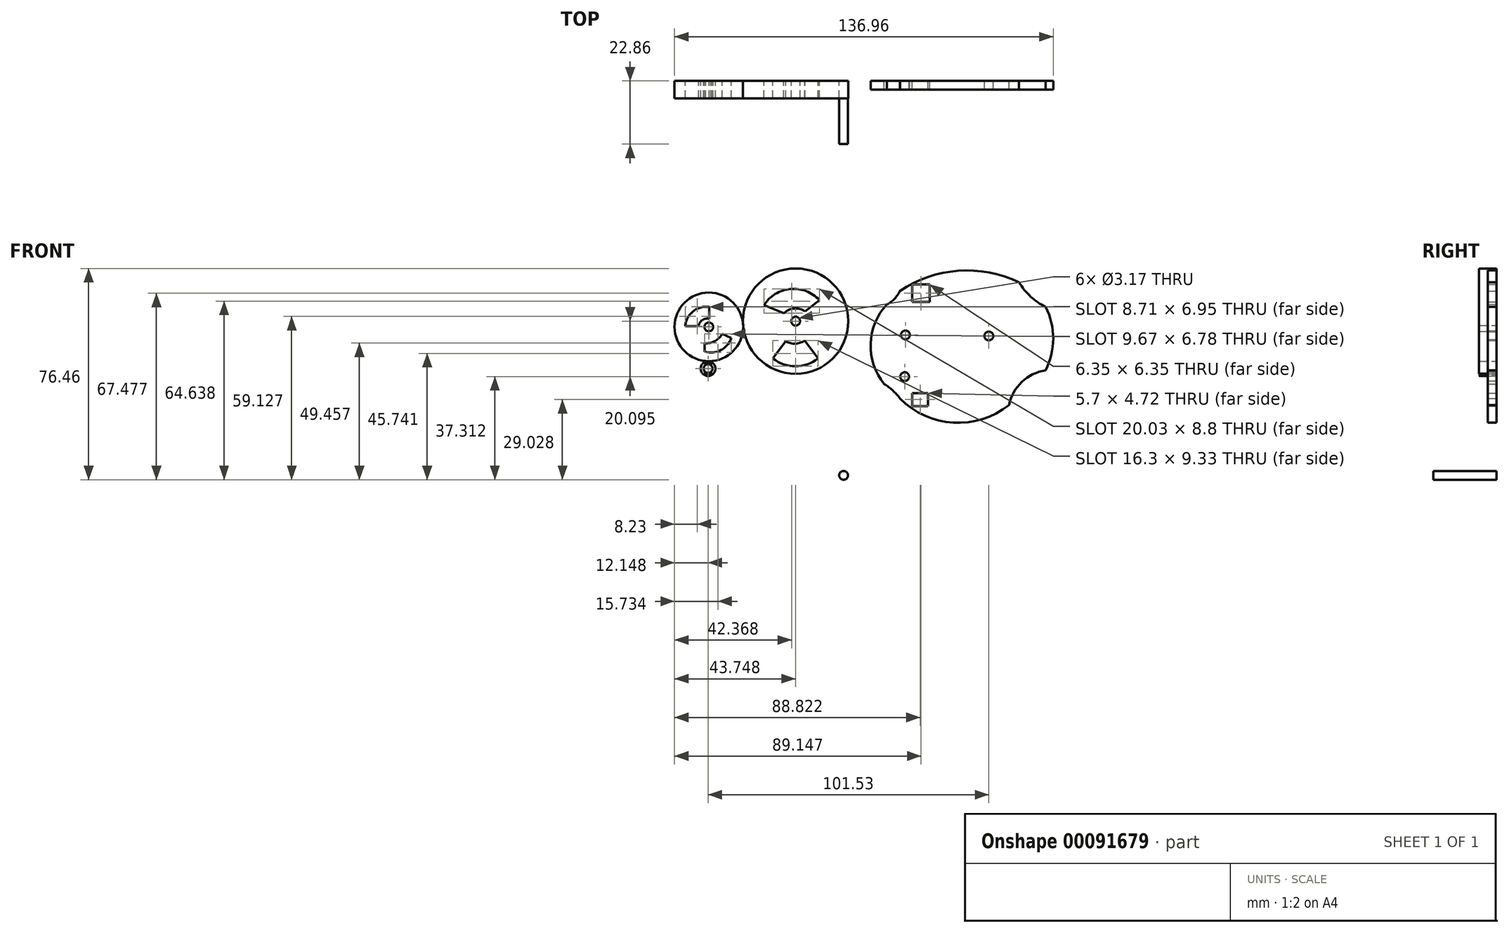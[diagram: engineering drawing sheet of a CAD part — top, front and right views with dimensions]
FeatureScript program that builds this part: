
annotation { "Feature Type Name" : "Feature", "Feature Type Description" : "" }
export const myFeature = defineFeature(function(context is Context, id is Id, definition is map)
    precondition{}
    {
        {
            var Q0;
            Q0=qCreatedBy(makeId("Front.planeOp"),FACE);
            var sketch = newSketch(context, id + "F0", { "sketchPlane" : qUnion([Q0])});
            skCircle(sketch, "E0", {"center": v(21.5, 8.13) * mm, "radius": 18.25 * mm});
            skCircle(sketch, "E1", {"center": v(-8.67, 8.5) * mm, "radius": 8.73 * mm});
            skCircle(sketch, "E2", {"center": v(-8.94, -6.58) * mm, "radius": 3.97 * mm});
            skCircle(sketch, "E3", {"center": v(-8.67, 8.5) * mm, "radius": 1.59 * mm});
            skCircle(sketch, "E4", {"center": v(-8.94, -6.58) * mm, "radius": 1.59 * mm});
            skCircle(sketch, "E5", {"center": v(21.5, 8.13) * mm, "radius": 1.59 * mm});
            skLineSegment(sketch, "E6", {"start": v(-8.94, -6.58) * mm, "end": v(-8.67, 8.5) * mm});
            skLineSegment(sketch, "E7", {"start": v(-8.67, 8.5) * mm, "end": v(21.5, 8.13) * mm});
            skArc(sketch, "E8", {"start": v(-10.62, -14.44) * mm, "mid": v(-13.24, -11.58) * mm, "end": v(-16.34, -9.24) * mm});
            skArc(sketch, "E9", {"start": v(-15.38, 19.52) * mm, "mid": v(-12.61, 21.57) * mm, "end": v(-10.7, 24.45) * mm});
            skArc(sketch, "E10", {"start": v(-15.38, 19.52) * mm, "mid": v(-21.24, 5.32) * mm, "end": v(-16.34, -9.24) * mm});
            skArc(sketch, "E11", {"start": v(32.45, 27.55) * mm, "mid": v(36.63, 22.41) * mm, "end": v(42.08, 18.63) * mm});
            skArc(sketch, "E12", {"start": v(42.02, -4.32) * mm, "mid": v(44.79, 7.15) * mm, "end": v(42.08, 18.63) * mm});
            skArc(sketch, "E13", {"start": v(32.45, 27.55) * mm, "mid": v(10.46, 31.73) * mm, "end": v(-10.7, 24.45) * mm});
            skArc(sketch, "E14", {"start": v(-10.62, -14.44) * mm, "mid": v(8.66, -23.23) * mm, "end": v(28.85, -16.81) * mm});
            skArc(sketch, "E15", {"start": v(42.02, -4.32) * mm, "mid": v(33.46, -8.48) * mm, "end": v(28.85, -16.81) * mm});
            skLineSegment(sketch, "E16.bottom", {"start": v(-6.2, 26.76) * mm, "end": v(0.15, 26.76) * mm});
            skLineSegment(sketch, "E16.top", {"start": v(-6.2, 20.41) * mm, "end": v(0.15, 20.41) * mm});
            skLineSegment(sketch, "E16.left", {"start": v(-6.2, 26.76) * mm, "end": v(-6.2, 20.41) * mm});
            skLineSegment(sketch, "E16.right", {"start": v(0.15, 26.76) * mm, "end": v(0.15, 20.41) * mm});
            skLineSegment(sketch, "E17.bottom", {"start": v(-6.2, -12.5) * mm, "end": v(-0.5, -12.5) * mm});
            skLineSegment(sketch, "E17.top", {"start": v(-6.2, -17.22) * mm, "end": v(-0.5, -17.22) * mm});
            skLineSegment(sketch, "E17.left", {"start": v(-6.2, -12.5) * mm, "end": v(-6.2, -17.22) * mm});
            skLineSegment(sketch, "E17.right", {"start": v(-0.5, -12.5) * mm, "end": v(-0.5, -17.22) * mm});
            skCircle(sketch, "E18", {"center": v(-48.35, 13.52) * mm, "radius": 19.05 * mm});
            skCircle(sketch, "E19", {"center": v(-79.75, 11.42) * mm, "radius": 12.42 * mm});
            skCircle(sketch, "E20", {"center": v(-80.02, -3.66) * mm, "radius": 2.67 * mm});
            skCircle(sketch, "E21", {"center": v(-79.75, 11.42) * mm, "radius": 1.59 * mm});
            skCircle(sketch, "E22", {"center": v(-80.02, -3.66) * mm, "radius": 1.59 * mm});
            skCircle(sketch, "E23", {"center": v(-48.35, 13.52) * mm, "radius": 1.59 * mm});
            skPoint(sketch, "E24.left.start.orphan", {"position": v(-74.67, -8.14) * mm});
            skPoint(sketch, "E25.left.end.orphan", {"position": v(-74.67, 22) * mm});
            skCircle(sketch, "E26", {"center": v(-45.36, -13.19) * mm, "radius": 1.59 * mm});
            skCircle(sketch, "E27", {"center": v(-31.02, -42.3) * mm, "radius": 1.59 * mm});
            skLineSegment(sketch, "E28", {"start": v(-88.3, 11.76) * mm, "end": v(-83.46, 11.76) * mm});
            skLineSegment(sketch, "E29", {"start": v(-79.59, 14.36) * mm, "end": v(-79.59, 18.64) * mm});
            skArc(sketch, "E30", {"start": v(-79.59, 18.64) * mm, "mid": v(-85.42, 17.08) * mm, "end": v(-88.3, 11.76) * mm});
            skArc(sketch, "E31", {"start": v(-79.59, 14.36) * mm, "mid": v(-82.1, 13.91) * mm, "end": v(-83.46, 11.76) * mm});
            skLineSegment(sketch, "E32", {"start": v(-81.27, 5.52) * mm, "end": v(-81.27, 2.48) * mm});
            skLineSegment(sketch, "E33", {"start": v(-74.9, 8.96) * mm, "end": v(-71.6, 7.43) * mm});
            skArc(sketch, "E34", {"start": v(-81.27, 5.52) * mm, "mid": v(-77.56, 6.26) * mm, "end": v(-74.9, 8.96) * mm});
            skArc(sketch, "E35", {"start": v(-81.27, 2.48) * mm, "mid": v(-75.44, 3) * mm, "end": v(-71.6, 7.43) * mm});
            skLineSegment(sketch, "E36", {"start": v(-59.82, 19.27) * mm, "end": v(-52.65, 16.35) * mm});
            skLineSegment(sketch, "E37", {"start": v(-44.91, 17.02) * mm, "end": v(-39.79, 21.15) * mm});
            skArc(sketch, "E38", {"start": v(-39.79, 21.15) * mm, "mid": v(-50.26, 25.15) * mm, "end": v(-59.82, 19.27) * mm});
            skArc(sketch, "E39", {"start": v(-44.91, 17.02) * mm, "mid": v(-48.9, 18.07) * mm, "end": v(-52.65, 16.35) * mm});
            skLineSegment(sketch, "E40", {"start": v(-52, 6.26) * mm, "end": v(-56.57, 0) * mm});
            skPoint(sketch, "E40.startSnap0", {"position": v(-77.56, 6.26) * mm});
            skLineSegment(sketch, "E41", {"start": v(-45.09, 6.51) * mm, "end": v(-40.27, 0) * mm});
            skArc(sketch, "E42", {"start": v(-52, 6.26) * mm, "mid": v(-48.5, 5.38) * mm, "end": v(-45.09, 6.51) * mm});
            skArc(sketch, "E43", {"start": v(-56.57, 0) * mm, "mid": v(-48.42, -2.81) * mm, "end": v(-40.27, 0) * mm});
            skLineSegment(sketch, "E44", {"start": v(-81.35, -1.7) * mm, "end": v(-80.86, -2.01) * mm});
            skLineSegment(sketch, "E45", {"start": v(-79.03, -2.06) * mm, "end": v(-78.63, -1.75) * mm});
            skArc(sketch, "E46", {"start": v(-78.63, -1.75) * mm, "mid": v(-79.98, -1.38) * mm, "end": v(-81.35, -1.7) * mm});
            skArc(sketch, "E47", {"start": v(-79.03, -2.06) * mm, "mid": v(-79.94, -1.84) * mm, "end": v(-80.86, -2.01) * mm});
            skLineSegment(sketch, "E48", {"start": v(-81.03, -5.32) * mm, "end": v(-81.5, -5.55) * mm});
            skLineSegment(sketch, "E49", {"start": v(-79.04, -5.3) * mm, "end": v(-78.54, -5.62) * mm});
            skArc(sketch, "E50", {"start": v(-81.03, -5.32) * mm, "mid": v(-80.03, -5.52) * mm, "end": v(-79.04, -5.3) * mm});
            skArc(sketch, "E51", {"start": v(-81.5, -5.55) * mm, "mid": v(-80.03, -6.02) * mm, "end": v(-78.54, -5.62) * mm});
            skSolve(sketch);
        }
        {
            var Q0;
            Q0=makeQuery(id+"F0.imprint","IMPRINT",FACE,{"disambiguationData":[TD([[makeQuery(id+"F0.imprint","IMPRINT",EDGE,{"derivedFrom":sQuery(id+"F0.wireOp",EDGE,"E18")}),1.0]])]});
            var Q1;
            Q1=makeQuery(id+"F0.imprint","IMPRINT",FACE,{"disambiguationData":[TD([[makeQuery(id+"F0.imprint","IMPRINT",EDGE,{"derivedFrom":sQuery(id+"F0.wireOp",EDGE,"E19")}),1.0]])]});
            var Q2;
            Q2=makeQuery(id+"F0.imprint","IMPRINT",FACE,{"disambiguationData":[TD([[makeQuery(id+"F0.imprint","IMPRINT",EDGE,{"derivedFrom":sQuery(id+"F0.wireOp",EDGE,"E20")}),1.0]])]});
            extrude(context, id + "F1", {"entities" : qUnion([Q0, Q1, Q2]), "depth" : 6.35 * mm});
        }
        {
            var Q0;
            Q0=makeQuery(id+"F0.imprint","IMPRINT",FACE,{"disambiguationData":[TD([[makeQuery(id+"F0.imprint","IMPRINT",EDGE,{"derivedFrom":sQuery(id+"F0.wireOp",EDGE,"E0")}),1.0]])]});
            var Q1;
            {var subQ0=sQuery(id+"F0.wireOp",EDGE,"E6");var subQ1=sQuery(id+"F0.wireOp",EDGE,"E1");var subQ2=makeQuery(id+"F0.imprint","INTERSECT",VERTEX,{"derivedFrom":[subQ1,subQ0]});Q1=makeQuery(id+"F0.imprint","IMPRINT",FACE,{"disambiguationData":[TD([[makeQuery(id+"F0.imprint","IMPRINT",EDGE,{"disambiguationData":[TD([[subQ2,1.0]])],"derivedFrom":subQ1}),1.0]])]});}
            var Q2;
            {var subQ0=sQuery(id+"F0.wireOp",EDGE,"E6");var subQ1=sQuery(id+"F0.wireOp",EDGE,"E1");var subQ2=makeQuery(id+"F0.imprint","INTERSECT",VERTEX,{"derivedFrom":[subQ1,subQ0]});Q2=makeQuery(id+"F0.imprint","IMPRINT",FACE,{"disambiguationData":[TD([[makeQuery(id+"F0.imprint","IMPRINT",EDGE,{"disambiguationData":[TD([[subQ2,-1.0]])],"derivedFrom":subQ1}),1.0]])]});}
            var Q3;
            Q3=makeQuery(id+"F0.imprint","IMPRINT",FACE,{"disambiguationData":[TD([[makeQuery(id+"F0.imprint","IMPRINT",EDGE,{"derivedFrom":sQuery(id+"F0.wireOp",EDGE,"E2")}),1.0]])]});
            var Q4;
            Q4=makeQuery(id+"F0.imprint","IMPRINT",FACE,{"disambiguationData":[TD([[makeQuery(id+"F0.imprint","IMPRINT",EDGE,{"derivedFrom":sQuery(id+"F0.wireOp",EDGE,"E0")}),-1.0]])]});
            extrude(context, id + "F2", {"entities" : qUnion([Q0, Q1, Q2, Q3, Q4]), "depth" : 3.17 * mm});
        }
        {
            var Q0;
            Q0=makeQuery(id+"F0.imprint","IMPRINT",FACE,{"disambiguationData":[TD([[makeQuery(id+"F0.imprint","IMPRINT",EDGE,{"derivedFrom":sQuery(id+"F0.wireOp",EDGE,"E27")}),1.0]])]});
            extrude(context, id + "F3", {"entities" : qUnion([Q0]), "depth" : 22.86 * mm});
        }
    });
